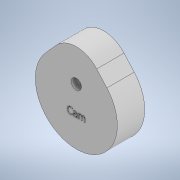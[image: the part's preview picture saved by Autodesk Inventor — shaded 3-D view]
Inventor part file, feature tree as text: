
AUTODESK INVENTOR PART (.ipt)
format: ipt  version: 2021 (Build 250183000, 183)  size: 247,296 bytes
history: native  units: mm
features: sketch x3, extrude x1, emboss x1, hole x1
ambient origin geometry x8: Origin, YZ Plane, XZ Plane, XY Plane, X Axis, Y Axis, Z Axis, Center Point
bodies: Solid1 (feature_tree)
feature tree (6):
  extrude  "Extrusion1"  Depth=6.0mm
  emboss  "Emboss1"
  hole  "Hole1"  [1 undecoded]
  sketch  "Sketch1"  dims[d0=24.0mm d1=6.0mm]
  sketch  "Sketch2"  dims[d2=16.0mm d3=5.0mm]
  sketch  "Sketch3"  dims[d4=4.5mm d5=8.0mm d6=0.0mm d9=1.0mm d10=0.0mm d11=5.0mm d12=4.5mm d13=3.0mm d14=6.0mm d15=4.0mm d16=2.0mm d17=90.0deg d18=8.0mm d19=20.594885mm d20=0.75mm d21=20.594885mm d22=0.0625mm d23=0.75mm d24=0.375mm]
note: 1 required parameter value undecoded (feature->parameter linkage not recoverable at this tier; creation-order binding heuristic only, values carry confidence <= 0.55)
